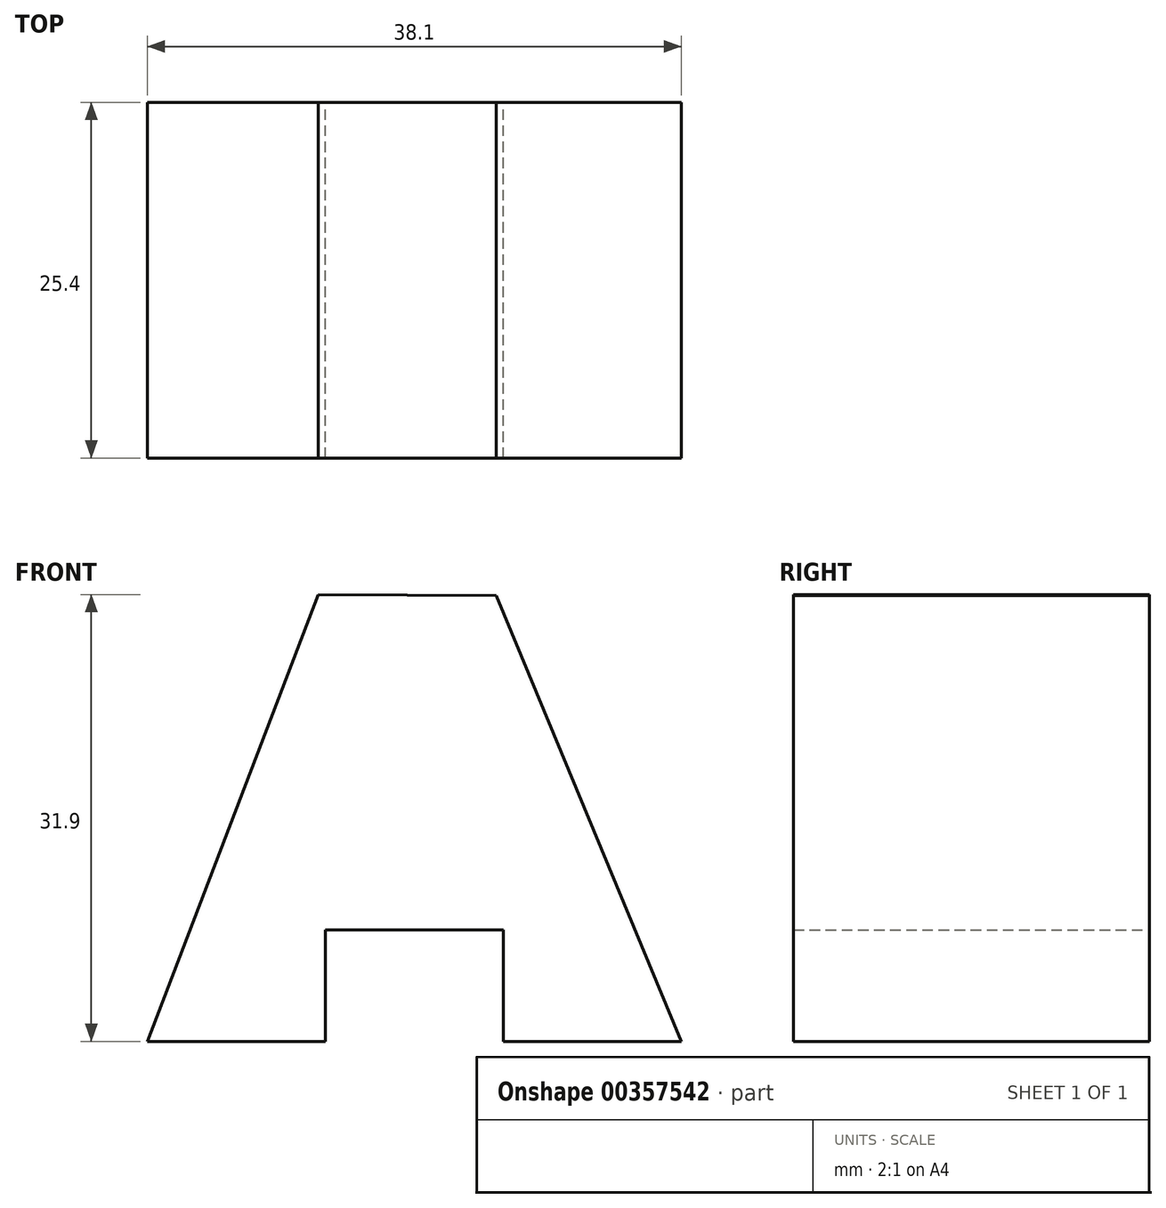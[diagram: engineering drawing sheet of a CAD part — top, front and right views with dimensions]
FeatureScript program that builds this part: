
annotation { "Feature Type Name" : "Feature", "Feature Type Description" : "" }
export const myFeature = defineFeature(function(context is Context, id is Id, definition is map)
    precondition{}
    {
        {
            var Q0;
            Q0=qCreatedBy(makeId("Front.planeOp"),FACE);
            var sketch = newSketch(context, id + "F0", { "sketchPlane" : qUnion([Q0])});
            skLineSegment(sketch, "E0", {"start": v(-32.78, 50.04) * mm, "end": v(-32.78, 18.06) * mm});
            skLineSegment(sketch, "E1", {"start": v(5.32, 18.06) * mm, "end": v(5.32, 49.8) * mm});
            skLineSegment(sketch, "E2", {"start": v(5.32, 49.8) * mm, "end": v(-32.78, 50.04) * mm});
            skLineSegment(sketch, "E3", {"start": v(-32.78, 18.06) * mm, "end": v(-20.08, 18.06) * mm});
            skLineSegment(sketch, "E4", {"start": v(-20.08, 18.06) * mm, "end": v(-20.08, 26.01) * mm});
            skLineSegment(sketch, "E5", {"start": v(-20.08, 26.01) * mm, "end": v(-7.38, 26.01) * mm});
            skLineSegment(sketch, "E6", {"start": v(-7.38, 26.01) * mm, "end": v(-7.38, 18.06) * mm});
            skLineSegment(sketch, "E7", {"start": v(-7.38, 18.06) * mm, "end": v(5.32, 18.06) * mm});
            skLineSegment(sketch, "E8", {"start": v(5.32, 18.06) * mm, "end": v(-7.9, 49.89) * mm});
            skLineSegment(sketch, "E9", {"start": v(-32.78, 18.06) * mm, "end": v(-20.6, 49.96) * mm});
            skLineSegment(sketch, "E10", {"start": v(-20.6, 49.96) * mm, "end": v(-7.9, 49.89) * mm});
            skSolve(sketch);
        }
        {
            var Q0;
            Q0=makeQuery(id+"F0.imprint","IMPRINT",FACE,{"disambiguationData":[TD([[makeQuery(id+"F0.imprint","IMPRINT",EDGE,{"derivedFrom":sQuery(id+"F0.wireOp",EDGE,"E3")}),1.0]])]});
            extrude(context, id + "F1", {"entities" : qUnion([Q0]), "depth" : 25.4 * mm});
        }
    });
